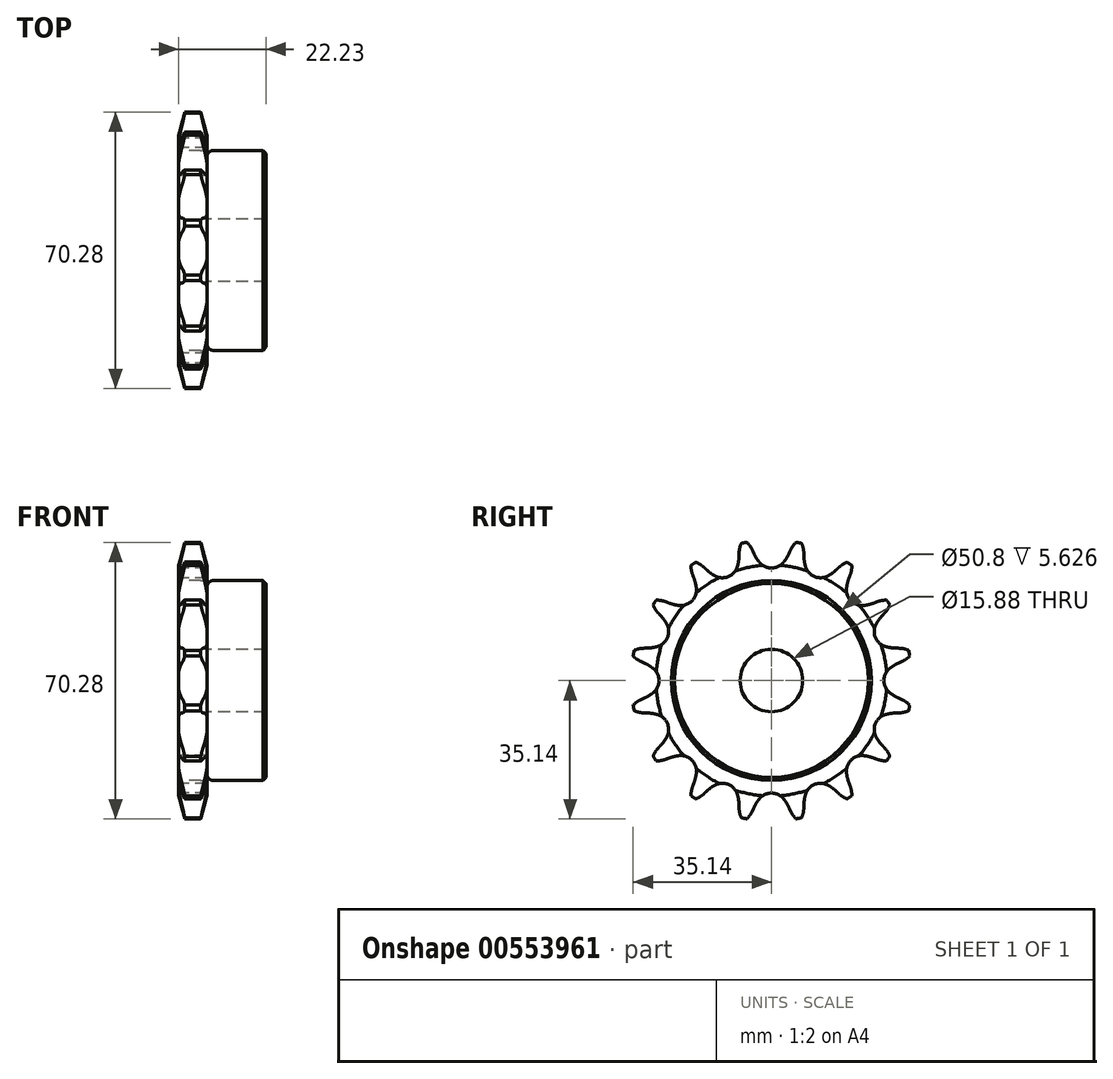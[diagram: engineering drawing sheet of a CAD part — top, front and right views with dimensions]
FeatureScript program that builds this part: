
annotation { "Feature Type Name" : "Feature", "Feature Type Description" : "" }
export const myFeature = defineFeature(function(context is Context, id is Id, definition is map)
    precondition{}
    {
        {
            var Q0;
            Q0=qCreatedBy(makeId("Front.planeOp"),FACE);
            var sketch = newSketch(context, id + "F0", { "sketchPlane" : qUnion([Q0])});
            skLineSegment(sketch, "E0", {"start": v(0, 0) * mm, "end": v(22.22, 0) * mm, "construction": true});
            skLineSegment(sketch, "E1.bottom", {"start": v(0, 7.94) * mm, "end": v(7.21, 7.94) * mm});
            skLineSegment(sketch, "E1.top", {"start": v(0, 35.69) * mm, "end": v(7.21, 35.69) * mm});
            skLineSegment(sketch, "E1.left", {"start": v(0, 7.94) * mm, "end": v(0, 35.69) * mm});
            skLineSegment(sketch, "E1.right", {"start": v(7.21, 7.94) * mm, "end": v(7.21, 35.69) * mm});
            skLineSegment(sketch, "E2.bottom", {"start": v(0, 7.94) * mm, "end": v(22.22, 7.94) * mm});
            skLineSegment(sketch, "E2.top", {"start": v(0, 25.4) * mm, "end": v(22.22, 25.4) * mm});
            skLineSegment(sketch, "E2.left", {"start": v(0, 7.94) * mm, "end": v(0, 25.4) * mm});
            skLineSegment(sketch, "E2.right", {"start": v(22.22, 7.94) * mm, "end": v(22.22, 25.4) * mm});
            skLineSegment(sketch, "E3.MirrorCS", {"start": v(0, -7.94) * mm, "end": v(7.21, -7.94) * mm});
            skLineSegment(sketch, "E4.MirrorCS", {"start": v(0, -35.69) * mm, "end": v(7.21, -35.69) * mm});
            skLineSegment(sketch, "E5.MirrorCS", {"start": v(0, -7.94) * mm, "end": v(0, -35.69) * mm});
            skLineSegment(sketch, "E6.MirrorCS", {"start": v(0, -25.4) * mm, "end": v(22.22, -25.4) * mm});
            skLineSegment(sketch, "E7.MirrorCS", {"start": v(7.21, -7.94) * mm, "end": v(7.21, -35.69) * mm});
            skLineSegment(sketch, "E8.MirrorCS", {"start": v(0, -7.94) * mm, "end": v(22.22, -7.94) * mm});
            skLineSegment(sketch, "E9.MirrorCS", {"start": v(22.22, -7.94) * mm, "end": v(22.22, -25.4) * mm});
            skLineSegment(sketch, "E10.MirrorCS", {"start": v(0, -7.94) * mm, "end": v(0, -25.4) * mm});
            skSolve(sketch);
        }
        {
            var Q0;
            {var subQ5=sQuery(id+"F0.wireOp",EDGE,"E2.right");Q0=makeQuery(id+"F0.imprint","IMPRINT",FACE,{"disambiguationData":[TD([[makeQuery(id+"F0.imprint","IMPRINT",EDGE,{"derivedFrom":subQ5}),1.0]])]});}
            var Q1;
            {var subQ5=sQuery(id+"F0.wireOp",EDGE,"E2.left");Q1=makeQuery(id+"F0.imprint","IMPRINT",FACE,{"disambiguationData":[TD([[makeQuery(id+"F0.imprint","IMPRINT",EDGE,{"derivedFrom":subQ5}),-1.0]])]});}
            var Q2;
            {var subQ0=sQuery(id+"F0.wireOp",EDGE,"E1.top");Q2=makeQuery(id+"F0.imprint","IMPRINT",FACE,{"disambiguationData":[TD([[makeQuery(id+"F0.imprint","IMPRINT",EDGE,{"derivedFrom":subQ0}),-1.0]])]});}
            var Q3;
            Q3=sQuery(id+"F0.wireOp",EDGE,"E0");
            revolve(context, id + "F1", {"entities" : qUnion([Q0, Q1, Q2]), "axis" : qUnion([Q3]), "revolveType" : RevolveType.FULL});
        }
        {
            var Q0;
            Q0=makeQuery(id+"F1.opRevolve","SWEPT_EDGE",EDGE,{"disambiguationData":[OSD([sQuery(id+"F0.wireOp",EDGE,"E1.right"),sQuery(id+"F0.wireOp",EDGE,"E2.top")])]});
            fillet(context, id + "F2", {"entities" : qUnion([Q0]), "radius" : 1.59 * mm, "tangentPropagation" : true, "allowEdgeOverflow" : false});
        }
        {
            var Q0;
            Q0=makeQuery(id+"F1.opRevolve","SWEPT_EDGE",EDGE,{"disambiguationData":[OSD([sQuery(id+"F0.wireOp",EDGE,"E2.top"),sQuery(id+"F0.wireOp",EDGE,"E2.right")])]});
            chamfer(context, id + "F3", {"entities" : qUnion([Q0]), "width" : 0.8 * mm, "tangentPropagation" : true});
        }
        {
            var Q0;
            Q0=makeQuery(id+"F1.opRevolve","SWEPT_EDGE",EDGE,{"disambiguationData":[OSD([sQuery(id+"F0.wireOp",EDGE,"E1.top"),sQuery(id+"F0.wireOp",EDGE,"E1.left")])]});
            var Q1;
            Q1=makeQuery(id+"F1.opRevolve","SWEPT_EDGE",EDGE,{"disambiguationData":[OSD([sQuery(id+"F0.wireOp",EDGE,"E1.top"),sQuery(id+"F0.wireOp",EDGE,"E1.right")])]});
            chamfer(context, id + "F4", {"entities" : qUnion([Q0, Q1]), "chamferType" : ChamferType.TWO_OFFSETS, "width1" : 6.35 * mm, "oppositeDirection" : false, "width2" : 1.57 * mm, "tangentPropagation" : true});
        }
        {
            var Q0;
            Q0=makeQuery(id+"F1.opRevolve","SWEPT_FACE",FACE,{"disambiguationData":[OSD([sQuery(id+"F0.wireOp",EDGE,"E1.left"),sQuery(id+"F0.wireOp",EDGE,"E2.left")])]});
            var sketch = newSketch(context, id + "F5", { "sketchPlane" : qUnion([Q0])});
            skCircle(sketch, "E11", {"center": v(0, 0) * mm, "radius": 32.55 * mm, "construction": true});
            skLineSegment(sketch, "E12", {"start": v(0, 0) * mm, "end": v(0, 32.55) * mm, "construction": true});
            skLineSegment(sketch, "E13", {"start": v(0, 32.55) * mm, "end": v(43.22, 32.55) * mm, "construction": true});
            skLineSegment(sketch, "E14", {"start": v(0, 32.55) * mm, "end": v(5, 36.56) * mm, "construction": true});
            skLineSegment(sketch, "E15", {"start": v(5, 36.56) * mm, "end": v(-4.46, 32.3) * mm, "construction": true});
            skLineSegment(sketch, "E16", {"start": v(-4.46, 32.3) * mm, "end": v(-4.46, 32.3) * mm});
            skLineSegment(sketch, "E17", {"start": v(0, 0) * mm, "end": v(-7.13, 35.85) * mm, "construction": true});
            skArc(sketch, "E18", {"start": v(-7.13, 35.85) * mm, "mid": v(-15.87, 26.15) * mm, "end": v(-4.82, 33.1) * mm, "construction": true});
            skArc(sketch, "E19", {"start": v(-4.82, 33.1) * mm, "mid": v(-5.78, 34.63) * mm, "end": v(-7.13, 35.85) * mm});
            skArc(sketch, "E20", {"start": v(-4.46, 32.3) * mm, "mid": v(-3.84, 31.14) * mm, "end": v(-3.1, 30.07) * mm});
            skArc(sketch, "E21", {"start": v(-3.1, 30.07) * mm, "mid": v(13.83, 41.97) * mm, "end": v(-4.46, 32.3) * mm, "construction": true});
            skLineSegment(sketch, "E22", {"start": v(-4.82, 33.1) * mm, "end": v(-4.82, 33.1) * mm});
            skLineSegment(sketch, "E23", {"start": v(-4.46, 32.3) * mm, "end": v(-4.82, 33.1) * mm});
            skArc(sketch, "E24.MirrorCS", {"start": v(4.46, 32.3) * mm, "mid": v(3.84, 31.14) * mm, "end": v(3.1, 30.07) * mm});
            skLineSegment(sketch, "E25.MirrorCS", {"start": v(4.46, 32.3) * mm, "end": v(4.82, 33.1) * mm});
            skArc(sketch, "E26.MirrorCS", {"start": v(4.82, 33.1) * mm, "mid": v(5.78, 34.63) * mm, "end": v(7.13, 35.85) * mm});
            skArc(sketch, "E27", {"start": v(-3.1, 30.07) * mm, "mid": v(0, 28.59) * mm, "end": v(3.1, 30.07) * mm});
            skArc(sketch, "E28", {"start": v(3.1, 30.07) * mm, "mid": v(0, 36.51) * mm, "end": v(-3.1, 30.07) * mm, "construction": true});
            skLineSegment(sketch, "E29", {"start": v(5.33, 10.58) * mm, "end": v(5.29, 10.67) * mm});
            skLineSegment(sketch, "E30", {"start": v(5.29, 10.67) * mm, "end": v(-4.46, 32.3) * mm, "construction": true});
            skArc(sketch, "E31.1.0", {"start": v(-17.12, 28.74) * mm, "mid": v(-18.6, 29.79) * mm, "end": v(-20.3, 30.4) * mm});
            skLineSegment(sketch, "E31.1.1", {"start": v(-16.48, 28.14) * mm, "end": v(-17.12, 28.74) * mm});
            skArc(sketch, "E31.1.2", {"start": v(-16.48, 28.14) * mm, "mid": v(-15.47, 27.3) * mm, "end": v(-14.36, 26.6) * mm});
            skArc(sketch, "E31.1.3", {"start": v(-14.36, 26.6) * mm, "mid": v(-10.94, 26.41) * mm, "end": v(-8.65, 28.96) * mm});
            skArc(sketch, "E31.1.4", {"start": v(-8.24, 31.55) * mm, "mid": v(-8.37, 30.24) * mm, "end": v(-8.65, 28.96) * mm});
            skLineSegment(sketch, "E31.1.5", {"start": v(-8.24, 31.55) * mm, "end": v(-8.22, 32.42) * mm});
            skArc(sketch, "E31.1.6", {"start": v(-8.22, 32.42) * mm, "mid": v(-7.91, 34.21) * mm, "end": v(-7.13, 35.85) * mm});
            skArc(sketch, "E31.2.0", {"start": v(-26.8, 20) * mm, "mid": v(-28.58, 20.4) * mm, "end": v(-30.4, 20.3) * mm});
            skLineSegment(sketch, "E31.2.1", {"start": v(-26, 19.69) * mm, "end": v(-26.8, 20) * mm});
            skArc(sketch, "E31.2.2", {"start": v(-26, 19.69) * mm, "mid": v(-24.74, 19.3) * mm, "end": v(-23.45, 19.08) * mm});
            skArc(sketch, "E31.2.3", {"start": v(-23.45, 19.08) * mm, "mid": v(-20.21, 20.21) * mm, "end": v(-19.08, 23.45) * mm});
            skArc(sketch, "E31.2.4", {"start": v(-19.69, 26) * mm, "mid": v(-19.3, 24.74) * mm, "end": v(-19.08, 23.45) * mm});
            skLineSegment(sketch, "E31.2.5", {"start": v(-19.69, 26) * mm, "end": v(-20, 26.8) * mm});
            skArc(sketch, "E31.2.6", {"start": v(-20, 26.8) * mm, "mid": v(-20.4, 28.58) * mm, "end": v(-20.3, 30.4) * mm});
            skArc(sketch, "E32.1.3.0", {"start": v(-32.42, 8.22) * mm, "mid": v(-34.21, 7.91) * mm, "end": v(-35.85, 7.13) * mm});
            skLineSegment(sketch, "E32.4.3.0", {"start": v(-31.55, 8.24) * mm, "end": v(-32.42, 8.22) * mm});
            skArc(sketch, "E32.7.3.0", {"start": v(-31.55, 8.24) * mm, "mid": v(-30.24, 8.37) * mm, "end": v(-28.96, 8.65) * mm});
            skArc(sketch, "E32.11.3.0", {"start": v(-28.96, 8.65) * mm, "mid": v(-26.41, 10.94) * mm, "end": v(-26.6, 14.36) * mm});
            skArc(sketch, "E32.15.3.0", {"start": v(-28.14, 16.48) * mm, "mid": v(-27.3, 15.47) * mm, "end": v(-26.6, 14.36) * mm});
            skLineSegment(sketch, "E32.19.3.0", {"start": v(-28.14, 16.48) * mm, "end": v(-28.74, 17.12) * mm});
            skArc(sketch, "E32.22.3.0", {"start": v(-28.74, 17.12) * mm, "mid": v(-29.79, 18.6) * mm, "end": v(-30.4, 20.3) * mm});
            skArc(sketch, "E32.1.4.0", {"start": v(-33.1, -4.82) * mm, "mid": v(-34.63, -5.78) * mm, "end": v(-35.85, -7.13) * mm});
            skLineSegment(sketch, "E32.4.4.0", {"start": v(-32.3, -4.46) * mm, "end": v(-33.1, -4.82) * mm});
            skArc(sketch, "E32.7.4.0", {"start": v(-32.3, -4.46) * mm, "mid": v(-31.14, -3.84) * mm, "end": v(-30.07, -3.1) * mm});
            skArc(sketch, "E32.11.4.0", {"start": v(-30.07, -3.1) * mm, "mid": v(-28.59, 0) * mm, "end": v(-30.07, 3.1) * mm});
            skArc(sketch, "E32.15.4.0", {"start": v(-32.3, 4.46) * mm, "mid": v(-31.14, 3.84) * mm, "end": v(-30.07, 3.1) * mm});
            skLineSegment(sketch, "E32.19.4.0", {"start": v(-32.3, 4.46) * mm, "end": v(-33.1, 4.82) * mm});
            skArc(sketch, "E32.22.4.0", {"start": v(-33.1, 4.82) * mm, "mid": v(-34.63, 5.78) * mm, "end": v(-35.85, 7.13) * mm});
            skArc(sketch, "E32.1.5.0", {"start": v(-28.74, -17.12) * mm, "mid": v(-29.79, -18.6) * mm, "end": v(-30.4, -20.3) * mm});
            skLineSegment(sketch, "E32.4.5.0", {"start": v(-28.14, -16.48) * mm, "end": v(-28.74, -17.12) * mm});
            skArc(sketch, "E32.7.5.0", {"start": v(-28.14, -16.48) * mm, "mid": v(-27.3, -15.47) * mm, "end": v(-26.6, -14.36) * mm});
            skArc(sketch, "E32.11.5.0", {"start": v(-26.6, -14.36) * mm, "mid": v(-26.41, -10.94) * mm, "end": v(-28.96, -8.65) * mm});
            skArc(sketch, "E32.15.5.0", {"start": v(-31.55, -8.24) * mm, "mid": v(-30.24, -8.37) * mm, "end": v(-28.96, -8.65) * mm});
            skLineSegment(sketch, "E32.19.5.0", {"start": v(-31.55, -8.24) * mm, "end": v(-32.42, -8.22) * mm});
            skArc(sketch, "E32.22.5.0", {"start": v(-32.42, -8.22) * mm, "mid": v(-34.21, -7.91) * mm, "end": v(-35.85, -7.13) * mm});
            skArc(sketch, "E32.1.6.0", {"start": v(-20, -26.8) * mm, "mid": v(-20.4, -28.58) * mm, "end": v(-20.3, -30.4) * mm});
            skLineSegment(sketch, "E32.4.6.0", {"start": v(-19.69, -26) * mm, "end": v(-20, -26.8) * mm});
            skArc(sketch, "E32.7.6.0", {"start": v(-19.69, -26) * mm, "mid": v(-19.3, -24.74) * mm, "end": v(-19.08, -23.45) * mm});
            skArc(sketch, "E32.11.6.0", {"start": v(-19.08, -23.45) * mm, "mid": v(-20.21, -20.21) * mm, "end": v(-23.45, -19.08) * mm});
            skArc(sketch, "E32.15.6.0", {"start": v(-26, -19.69) * mm, "mid": v(-24.74, -19.3) * mm, "end": v(-23.45, -19.08) * mm});
            skLineSegment(sketch, "E32.19.6.0", {"start": v(-26, -19.69) * mm, "end": v(-26.8, -20) * mm});
            skArc(sketch, "E32.22.6.0", {"start": v(-26.8, -20) * mm, "mid": v(-28.58, -20.4) * mm, "end": v(-30.4, -20.3) * mm});
            skArc(sketch, "E32.1.7.0", {"start": v(-8.22, -32.42) * mm, "mid": v(-7.91, -34.21) * mm, "end": v(-7.13, -35.85) * mm});
            skLineSegment(sketch, "E32.4.7.0", {"start": v(-8.24, -31.55) * mm, "end": v(-8.22, -32.42) * mm});
            skArc(sketch, "E32.7.7.0", {"start": v(-8.24, -31.55) * mm, "mid": v(-8.37, -30.24) * mm, "end": v(-8.65, -28.96) * mm});
            skArc(sketch, "E32.11.7.0", {"start": v(-8.65, -28.96) * mm, "mid": v(-10.94, -26.41) * mm, "end": v(-14.36, -26.6) * mm});
            skArc(sketch, "E32.15.7.0", {"start": v(-16.48, -28.14) * mm, "mid": v(-15.47, -27.3) * mm, "end": v(-14.36, -26.6) * mm});
            skLineSegment(sketch, "E32.19.7.0", {"start": v(-16.48, -28.14) * mm, "end": v(-17.12, -28.74) * mm});
            skArc(sketch, "E32.22.7.0", {"start": v(-17.12, -28.74) * mm, "mid": v(-18.6, -29.79) * mm, "end": v(-20.3, -30.4) * mm});
            skArc(sketch, "E32.1.8.0", {"start": v(4.82, -33.1) * mm, "mid": v(5.78, -34.63) * mm, "end": v(7.13, -35.85) * mm});
            skLineSegment(sketch, "E32.4.8.0", {"start": v(4.46, -32.3) * mm, "end": v(4.82, -33.1) * mm});
            skArc(sketch, "E32.7.8.0", {"start": v(4.46, -32.3) * mm, "mid": v(3.84, -31.14) * mm, "end": v(3.1, -30.07) * mm});
            skArc(sketch, "E32.11.8.0", {"start": v(3.1, -30.07) * mm, "mid": v(0, -28.59) * mm, "end": v(-3.1, -30.07) * mm});
            skArc(sketch, "E32.15.8.0", {"start": v(-4.46, -32.3) * mm, "mid": v(-3.84, -31.14) * mm, "end": v(-3.1, -30.07) * mm});
            skLineSegment(sketch, "E32.19.8.0", {"start": v(-4.46, -32.3) * mm, "end": v(-4.82, -33.1) * mm});
            skArc(sketch, "E32.22.8.0", {"start": v(-4.82, -33.1) * mm, "mid": v(-5.78, -34.63) * mm, "end": v(-7.13, -35.85) * mm});
            skArc(sketch, "E32.1.9.0", {"start": v(17.12, -28.74) * mm, "mid": v(18.6, -29.79) * mm, "end": v(20.3, -30.4) * mm});
            skLineSegment(sketch, "E32.4.9.0", {"start": v(16.48, -28.14) * mm, "end": v(17.12, -28.74) * mm});
            skArc(sketch, "E32.7.9.0", {"start": v(16.48, -28.14) * mm, "mid": v(15.47, -27.3) * mm, "end": v(14.36, -26.6) * mm});
            skArc(sketch, "E32.11.9.0", {"start": v(14.36, -26.6) * mm, "mid": v(10.94, -26.41) * mm, "end": v(8.65, -28.96) * mm});
            skArc(sketch, "E32.15.9.0", {"start": v(8.24, -31.55) * mm, "mid": v(8.37, -30.24) * mm, "end": v(8.65, -28.96) * mm});
            skLineSegment(sketch, "E32.19.9.0", {"start": v(8.24, -31.55) * mm, "end": v(8.22, -32.42) * mm});
            skArc(sketch, "E32.22.9.0", {"start": v(8.22, -32.42) * mm, "mid": v(7.91, -34.21) * mm, "end": v(7.13, -35.85) * mm});
            skArc(sketch, "E32.1.10.0", {"start": v(26.8, -20) * mm, "mid": v(28.58, -20.4) * mm, "end": v(30.4, -20.3) * mm});
            skLineSegment(sketch, "E32.4.10.0", {"start": v(26, -19.69) * mm, "end": v(26.8, -20) * mm});
            skArc(sketch, "E32.7.10.0", {"start": v(26, -19.69) * mm, "mid": v(24.74, -19.3) * mm, "end": v(23.45, -19.08) * mm});
            skArc(sketch, "E32.11.10.0", {"start": v(23.45, -19.08) * mm, "mid": v(20.21, -20.21) * mm, "end": v(19.08, -23.45) * mm});
            skArc(sketch, "E32.15.10.0", {"start": v(19.69, -26) * mm, "mid": v(19.3, -24.74) * mm, "end": v(19.08, -23.45) * mm});
            skLineSegment(sketch, "E32.19.10.0", {"start": v(19.69, -26) * mm, "end": v(20, -26.8) * mm});
            skArc(sketch, "E32.22.10.0", {"start": v(20, -26.8) * mm, "mid": v(20.4, -28.58) * mm, "end": v(20.3, -30.4) * mm});
            skArc(sketch, "E32.1.11.0", {"start": v(32.42, -8.22) * mm, "mid": v(34.21, -7.91) * mm, "end": v(35.85, -7.13) * mm});
            skLineSegment(sketch, "E32.4.11.0", {"start": v(31.55, -8.24) * mm, "end": v(32.42, -8.22) * mm});
            skArc(sketch, "E32.7.11.0", {"start": v(31.55, -8.24) * mm, "mid": v(30.24, -8.37) * mm, "end": v(28.96, -8.65) * mm});
            skArc(sketch, "E32.11.11.0", {"start": v(28.96, -8.65) * mm, "mid": v(26.41, -10.94) * mm, "end": v(26.6, -14.36) * mm});
            skArc(sketch, "E32.15.11.0", {"start": v(28.14, -16.48) * mm, "mid": v(27.3, -15.47) * mm, "end": v(26.6, -14.36) * mm});
            skLineSegment(sketch, "E32.19.11.0", {"start": v(28.14, -16.48) * mm, "end": v(28.74, -17.12) * mm});
            skArc(sketch, "E32.22.11.0", {"start": v(28.74, -17.12) * mm, "mid": v(29.79, -18.6) * mm, "end": v(30.4, -20.3) * mm});
            skArc(sketch, "E32.1.12.0", {"start": v(33.1, 4.82) * mm, "mid": v(34.63, 5.78) * mm, "end": v(35.85, 7.13) * mm});
            skLineSegment(sketch, "E32.4.12.0", {"start": v(32.3, 4.46) * mm, "end": v(33.1, 4.82) * mm});
            skArc(sketch, "E32.7.12.0", {"start": v(32.3, 4.46) * mm, "mid": v(31.14, 3.84) * mm, "end": v(30.07, 3.1) * mm});
            skArc(sketch, "E32.11.12.0", {"start": v(30.07, 3.1) * mm, "mid": v(28.59, 0) * mm, "end": v(30.07, -3.1) * mm});
            skArc(sketch, "E32.15.12.0", {"start": v(32.3, -4.46) * mm, "mid": v(31.14, -3.84) * mm, "end": v(30.07, -3.1) * mm});
            skLineSegment(sketch, "E32.19.12.0", {"start": v(32.3, -4.46) * mm, "end": v(33.1, -4.82) * mm});
            skArc(sketch, "E32.22.12.0", {"start": v(33.1, -4.82) * mm, "mid": v(34.63, -5.78) * mm, "end": v(35.85, -7.13) * mm});
            skArc(sketch, "E32.1.13.0", {"start": v(28.74, 17.12) * mm, "mid": v(29.79, 18.6) * mm, "end": v(30.4, 20.3) * mm});
            skLineSegment(sketch, "E32.4.13.0", {"start": v(28.14, 16.48) * mm, "end": v(28.74, 17.12) * mm});
            skArc(sketch, "E32.7.13.0", {"start": v(28.14, 16.48) * mm, "mid": v(27.3, 15.47) * mm, "end": v(26.6, 14.36) * mm});
            skArc(sketch, "E32.11.13.0", {"start": v(26.6, 14.36) * mm, "mid": v(26.41, 10.94) * mm, "end": v(28.96, 8.65) * mm});
            skArc(sketch, "E32.15.13.0", {"start": v(31.55, 8.24) * mm, "mid": v(30.24, 8.37) * mm, "end": v(28.96, 8.65) * mm});
            skLineSegment(sketch, "E32.19.13.0", {"start": v(31.55, 8.24) * mm, "end": v(32.42, 8.22) * mm});
            skArc(sketch, "E32.22.13.0", {"start": v(32.42, 8.22) * mm, "mid": v(34.21, 7.91) * mm, "end": v(35.85, 7.13) * mm});
            skArc(sketch, "E32.1.14.0", {"start": v(20, 26.8) * mm, "mid": v(20.4, 28.58) * mm, "end": v(20.3, 30.4) * mm});
            skLineSegment(sketch, "E32.4.14.0", {"start": v(19.69, 26) * mm, "end": v(20, 26.8) * mm});
            skArc(sketch, "E32.7.14.0", {"start": v(19.69, 26) * mm, "mid": v(19.3, 24.74) * mm, "end": v(19.08, 23.45) * mm});
            skArc(sketch, "E32.11.14.0", {"start": v(19.08, 23.45) * mm, "mid": v(20.21, 20.21) * mm, "end": v(23.45, 19.08) * mm});
            skArc(sketch, "E32.15.14.0", {"start": v(26, 19.69) * mm, "mid": v(24.74, 19.3) * mm, "end": v(23.45, 19.08) * mm});
            skLineSegment(sketch, "E32.19.14.0", {"start": v(26, 19.69) * mm, "end": v(26.8, 20) * mm});
            skArc(sketch, "E32.22.14.0", {"start": v(26.8, 20) * mm, "mid": v(28.58, 20.4) * mm, "end": v(30.4, 20.3) * mm});
            skArc(sketch, "E32.1.15.0", {"start": v(8.22, 32.42) * mm, "mid": v(7.91, 34.21) * mm, "end": v(7.13, 35.85) * mm});
            skLineSegment(sketch, "E32.4.15.0", {"start": v(8.24, 31.55) * mm, "end": v(8.22, 32.42) * mm});
            skArc(sketch, "E32.7.15.0", {"start": v(8.24, 31.55) * mm, "mid": v(8.37, 30.24) * mm, "end": v(8.65, 28.96) * mm});
            skArc(sketch, "E32.11.15.0", {"start": v(8.65, 28.96) * mm, "mid": v(10.94, 26.41) * mm, "end": v(14.36, 26.6) * mm});
            skArc(sketch, "E32.15.15.0", {"start": v(16.48, 28.14) * mm, "mid": v(15.47, 27.3) * mm, "end": v(14.36, 26.6) * mm});
            skLineSegment(sketch, "E32.19.15.0", {"start": v(16.48, 28.14) * mm, "end": v(17.12, 28.74) * mm});
            skArc(sketch, "E32.22.15.0", {"start": v(17.12, 28.74) * mm, "mid": v(18.6, 29.79) * mm, "end": v(20.3, 30.4) * mm});
            skSolve(sketch);
        }
        {
            var Q0;
            Q0 = qSketchRegion(id + "F5", true);
            extrude(context, id + "F6", {"entities" : qUnion([Q0]), "operationType" : NewBodyOperationType.INTERSECT, "endBound" : BoundingType.THROUGH_ALL, "oppositeDirection" : true, "depth" : 25.4 * mm, "offsetDistance" : 25.4 * mm});
        }
    });
